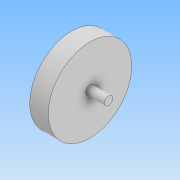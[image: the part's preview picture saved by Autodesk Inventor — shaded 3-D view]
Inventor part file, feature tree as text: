
AUTODESK INVENTOR PART (.ipt)
format: ipt  version: 2021 (Build 250183000, 183)  size: 83,968 bytes
history: native  units: mm
features: extrude x2, other x1, sketch x1
ambient origin geometry x8: Origin, YZ Plane, XZ Plane, XY Plane, X Axis, Y Axis, Z Axis, Center Point
bodies: Body1 (feature_tree)
feature tree (4):
  other  "實體1"
  sketch  "草圖1"
  extrude  "擠出1"  Depth=45.0mm
  extrude  "擠出2"  Depth=450.0mm
